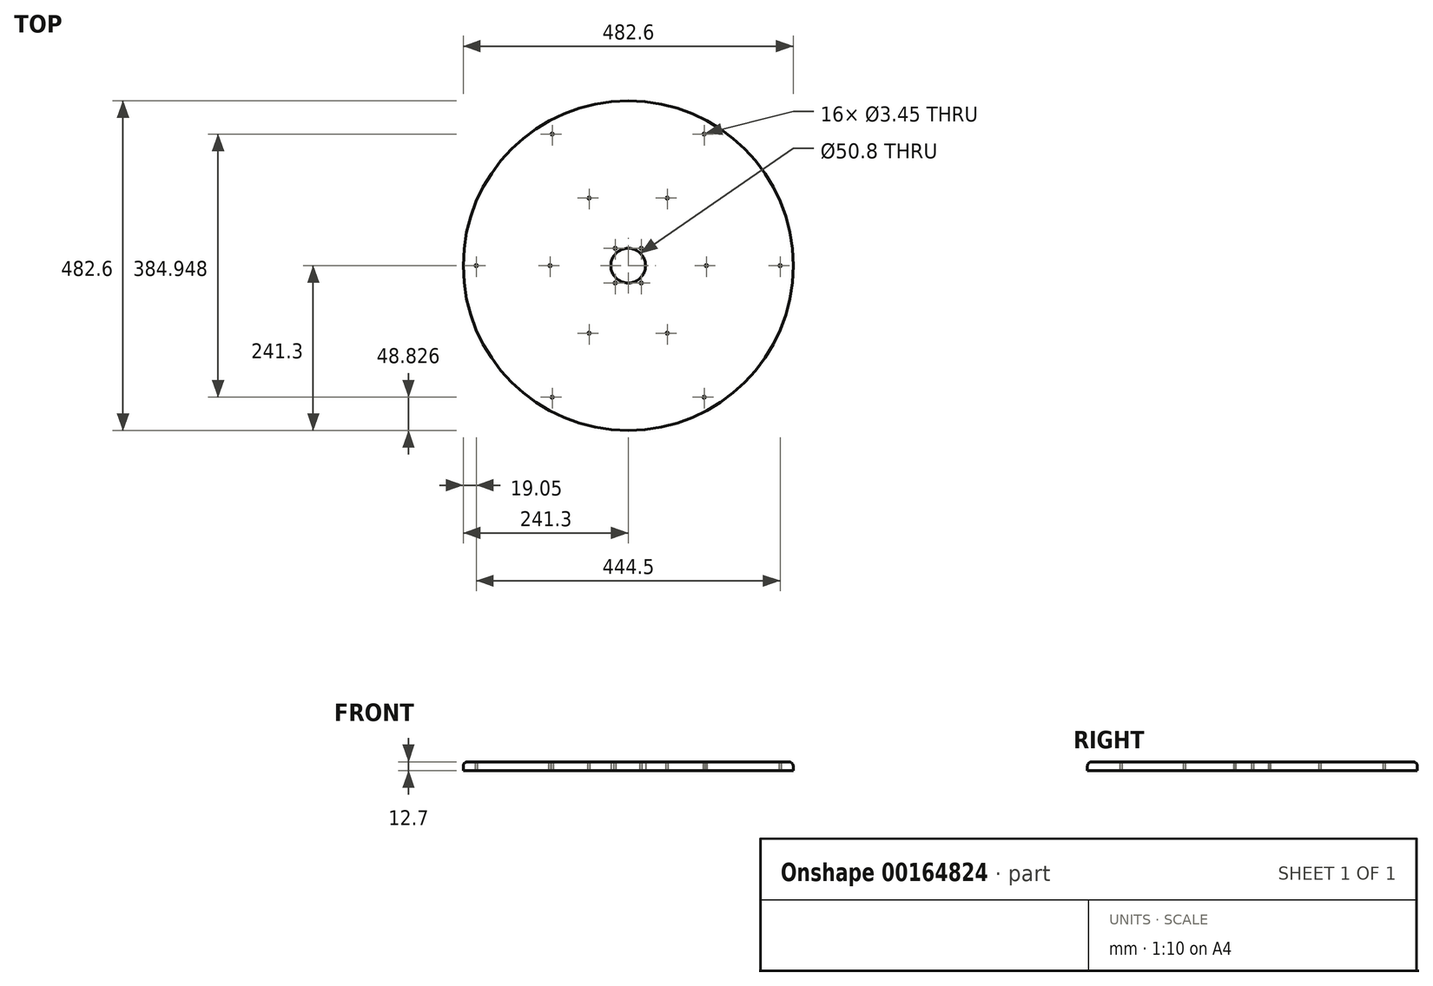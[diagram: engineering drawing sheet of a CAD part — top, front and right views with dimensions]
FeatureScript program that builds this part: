
annotation { "Feature Type Name" : "Feature", "Feature Type Description" : "" }
export const myFeature = defineFeature(function(context is Context, id is Id, definition is map)
    precondition{}
    {
        {
            var Q0;
            Q0=qCreatedBy(makeId("Top.planeOp"),FACE);
            var sketch = newSketch(context, id + "F0", { "sketchPlane" : qUnion([Q0])});
            skCircle(sketch, "E0", {"center": v(0, 0) * mm, "radius": 241.3 * mm});
            skCircle(sketch, "E1", {"center": v(0, 0) * mm, "radius": 25.4 * mm});
            skCircle(sketch, "E2.cCircle", {"center": v(0, 0) * mm, "radius": 192.47 * mm, "construction": true});
            skLineSegment(sketch, "E2.0", {"start": v(-111.12, 192.47) * mm, "end": v(111.12, 192.47) * mm, "construction": true});
            skLineSegment(sketch, "E2.1", {"start": v(111.12, 192.47) * mm, "end": v(222.25, 0) * mm, "construction": true});
            skLineSegment(sketch, "E2.2", {"start": v(222.25, 0) * mm, "end": v(111.12, -192.47) * mm, "construction": true});
            skLineSegment(sketch, "E2.3", {"start": v(111.13, -192.47) * mm, "end": v(-111.12, -192.47) * mm, "construction": true});
            skLineSegment(sketch, "E2.4", {"start": v(-111.12, -192.47) * mm, "end": v(-222.25, 0) * mm, "construction": true});
            skLineSegment(sketch, "E2.5", {"start": v(-222.25, 0) * mm, "end": v(-111.12, 192.47) * mm, "construction": true});
            skCircle(sketch, "E3", {"center": v(111.12, 192.47) * mm, "radius": 19.05 * mm, "construction": true});
            skCircle(sketch, "E4", {"center": v(111.12, 192.47) * mm, "radius": 1.73 * mm});
            skCircle(sketch, "E5", {"center": v(222.25, 0) * mm, "radius": 1.73 * mm});
            skCircle(sketch, "E6", {"center": v(111.12, -192.47) * mm, "radius": 1.73 * mm});
            skCircle(sketch, "E7", {"center": v(-111.12, -192.47) * mm, "radius": 1.73 * mm});
            skCircle(sketch, "E8", {"center": v(-222.25, 0) * mm, "radius": 1.73 * mm});
            skCircle(sketch, "E9", {"center": v(-111.12, 192.47) * mm, "radius": 1.73 * mm});
            skSolve(sketch);
        }
        {
            var Q0;
            Q0=qSketchRegion(id+"F0",true);
            extrude(context, id + "F1", {"entities" : qUnion([Q0]), "depth" : 12.7 * mm});
        }
        {
            var Q0;
            Q0=makeQuery(id+"F1.opExtrude","CAP_FACE",FACE,{"disambiguationData":[OSD([sQuery(id+"F0.wireOp",EDGE,"E0"),sQuery(id+"F0.wireOp",EDGE,"E1"),sQuery(id+"F0.wireOp",EDGE,"E4"),sQuery(id+"F0.wireOp",EDGE,"E5"),sQuery(id+"F0.wireOp",EDGE,"E6"),sQuery(id+"F0.wireOp",EDGE,"E7"),sQuery(id+"F0.wireOp",EDGE,"E8"),sQuery(id+"F0.wireOp",EDGE,"E9")])],"isStart":false});
            var sketch = newSketch(context, id + "F2", { "sketchPlane" : qUnion([Q0])});
            skCircle(sketch, "E10.cCircle", {"center": v(0, 0) * mm, "radius": 98.99 * mm, "construction": true});
            skLineSegment(sketch, "E10.0", {"start": v(-57.15, 98.99) * mm, "end": v(57.15, 98.99) * mm, "construction": true});
            skLineSegment(sketch, "E10.1", {"start": v(57.15, 98.99) * mm, "end": v(114.3, 0) * mm, "construction": true});
            skLineSegment(sketch, "E10.2", {"start": v(114.3, 0) * mm, "end": v(57.15, -98.99) * mm, "construction": true});
            skLineSegment(sketch, "E10.3", {"start": v(57.15, -98.99) * mm, "end": v(-57.15, -98.99) * mm, "construction": true});
            skLineSegment(sketch, "E10.4", {"start": v(-57.15, -98.99) * mm, "end": v(-114.3, 0) * mm, "construction": true});
            skLineSegment(sketch, "E10.5", {"start": v(-114.3, 0) * mm, "end": v(-57.15, 98.99) * mm, "construction": true});
            skCircle(sketch, "E11", {"center": v(0, 0) * mm, "radius": 127 * mm, "construction": true});
            skCircle(sketch, "E12", {"center": v(57.15, 98.99) * mm, "radius": 12.7 * mm, "construction": true});
            skCircle(sketch, "E13", {"center": v(-57.15, 98.99) * mm, "radius": 1.73 * mm});
            skCircle(sketch, "E14", {"center": v(57.15, 98.99) * mm, "radius": 1.73 * mm});
            skCircle(sketch, "E15", {"center": v(-114.3, 0) * mm, "radius": 1.73 * mm});
            skCircle(sketch, "E16", {"center": v(-57.15, -98.99) * mm, "radius": 1.73 * mm});
            skCircle(sketch, "E17", {"center": v(57.15, -98.99) * mm, "radius": 1.73 * mm});
            skCircle(sketch, "E18", {"center": v(114.3, 0) * mm, "radius": 1.73 * mm});
            skLineSegment(sketch, "E19.bottom", {"start": v(19.05, -25.4) * mm, "end": v(-19.05, -25.4) * mm, "construction": true});
            skLineSegment(sketch, "E19.top", {"start": v(19.05, 25.4) * mm, "end": v(-19.05, 25.4) * mm, "construction": true});
            skLineSegment(sketch, "E19.left", {"start": v(19.05, -25.4) * mm, "end": v(19.05, 25.4) * mm, "construction": true});
            skLineSegment(sketch, "E19.right", {"start": v(-19.05, -25.4) * mm, "end": v(-19.05, 25.4) * mm, "construction": true});
            skCircle(sketch, "E20", {"center": v(-19.05, -25.4) * mm, "radius": 6.35 * mm, "construction": true});
            skLineSegment(sketch, "E21.bottom", {"start": v(-25.4, -31.75) * mm, "end": v(25.4, -31.75) * mm, "construction": true});
            skLineSegment(sketch, "E21.top", {"start": v(-25.4, 31.75) * mm, "end": v(25.4, 31.75) * mm, "construction": true});
            skLineSegment(sketch, "E21.left", {"start": v(-25.4, -31.75) * mm, "end": v(-25.4, 31.75) * mm, "construction": true});
            skLineSegment(sketch, "E21.right", {"start": v(25.4, -31.75) * mm, "end": v(25.4, 31.75) * mm, "construction": true});
            skCircle(sketch, "E22", {"center": v(-19.05, -25.4) * mm, "radius": 1.73 * mm});
            skCircle(sketch, "E23", {"center": v(19.05, -25.4) * mm, "radius": 1.73 * mm});
            skCircle(sketch, "E24", {"center": v(19.05, 25.4) * mm, "radius": 1.73 * mm});
            skCircle(sketch, "E25", {"center": v(-19.05, 25.4) * mm, "radius": 1.73 * mm});
            skSolve(sketch);
        }
        {
            var Q0;
            Q0 = qSketchRegion(id + "F2", true);
            var Q1;
            Q1=makeQuery(id+"F1.opExtrude","CAP_FACE",FACE,{"disambiguationData":[OSD([sQuery(id+"F0.wireOp",EDGE,"E0"),sQuery(id+"F0.wireOp",EDGE,"E1"),sQuery(id+"F0.wireOp",EDGE,"E4"),sQuery(id+"F0.wireOp",EDGE,"E5"),sQuery(id+"F0.wireOp",EDGE,"E6"),sQuery(id+"F0.wireOp",EDGE,"E7"),sQuery(id+"F0.wireOp",EDGE,"E8"),sQuery(id+"F0.wireOp",EDGE,"E9")])],"isStart":true});
            extrude(context, id + "F3", {"entities" : qUnion([Q0]), "operationType" : NewBodyOperationType.REMOVE, "endBound" : BoundingType.UP_TO_SURFACE, "oppositeDirection" : true, "endBoundEntityFace" : qUnion([Q1]), "depth" : 25.4 * mm});
        }
        {
            var Q0;
            Q0=makeQuery(id+"F1.opExtrude","CAP_EDGE",EDGE,{"disambiguationData":[OSD([sQuery(id+"F0.wireOp",EDGE,"E0")])],"isStart":false});
            fillet(context, id + "F4", {"entities" : qUnion([Q0]), "radius" : 6.35 * mm, "tangentPropagation" : true, "allowEdgeOverflow" : false});
        }
    });
